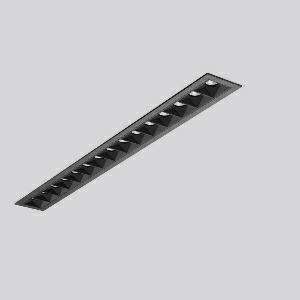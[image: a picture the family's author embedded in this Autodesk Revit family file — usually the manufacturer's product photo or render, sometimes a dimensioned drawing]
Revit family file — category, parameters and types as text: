
# Revit family: beamline_slim_641330_003_1_0f59
name_source: partatom
category: Lighting Fixtures
units: mm (PartAtom-declared; Revit-internal decimal feet)

## family parameters
Cut with Voids When Loaded = No
Host = Face
Light Source = No
Part Type = Normal
Room Calculation Point = No
Round Connector Dimension = Use Diameter
Shared = No

## types (1)
- BEAMLINE SLIM (1 x LED Modul 930, 3050 lm, 3000)
    Apparent Load = 36 VA
    CIE Flux Codes = 100 100 100 100 100
    Color Rendering = 90
    Color Temperature = 3000
    Default Elevation = 1800 mm
    Description = Series: BEAMLINE SLIM
Minimalistic recessed ceiling luminaire for aesthetically sophisticated lighting. Housing: metal, powder-coated. Perfect heat management with an aluminium heat sink. LED light unit with MRS technology: Mini-Reflector-System made of metallised thermoplastic with prismatic black glare-suppressing frame for pleasant glare-free light (RUG < 10). Medium beam light distribution. Ceiling installation with spring system. Including separate LED converter with connecting cable 450 mm. 
Colour: deep black, matt (RAL 9005)
Length: 435 mm
Width: 45 mm
Height: 1.5 mm
Cut-out length: 430 mm
Cut-out width: 40 mm
Recess height: 110 mm
Luminaire: recess height: 60 mm
Lamp: LED
Socket: without socket
Colour temperature: 3000K
Colour rendering index (CRI): 90
System power: 36 W
Rated luminous flux: 3050 lm
Luminous efficiency: 85 lm/W
Control gear: Regulated power supply
Protection class: II
Type of protection: IP 20
    Height = 0 mm  [stored 0 ft]
    Lamp = 1 x LED Modul 930
    Lamp Light Flux = 3050 lm
    Lamp count = 1
    Length = 435 mm
    Lifetime = 50000 h
    Luminous efficacy = 85 lm/W
    Manufacturer = RZB
    ModVariant = No
    Model = 641330.003.1
    Mounting Place = Ceiling
    Mounting Type = Recessed
    Number of Poles = 1
    OnlyDefault = Yes
    Power Factor = 1
    Product Name = BEAMLINE SLIM
    Product group = Recessed LED linear luminaires
    ProductGroupID = 407
    Protection Class = Protection class II
    Protection Degree = IP 20
    RLX_Detail_Level = 1
    RLX_Emergency_Light_Flux = 0 lm
    RLX_Emergency_Type = 0
    RLX_Emergency_Type_DB = No
    RlxData = <blob elided: 19917 chars, md5=7fd76be6>
    Socket = socket
    Standby Power = 0 W
    System Light Flux = 3050 lm
    System Power = 36 W
    Type Comments = Product without accessories
    Type Image = 641329.003.jpg
    URL = http://relux.com
    VarID = ---
    Voltage = 230 V
    Voltage Range = 220-240 V
    Weight = 0.00 kg
    Width = 45 mm

note: [stored X ft] marks values corroborated as IEEE doubles in the binary element streams (Revit-internal decimal feet)

## geometry (parser evidence)
native form markers: Blend x4, Sweep x13
no freeform markers — native parametric forms only
